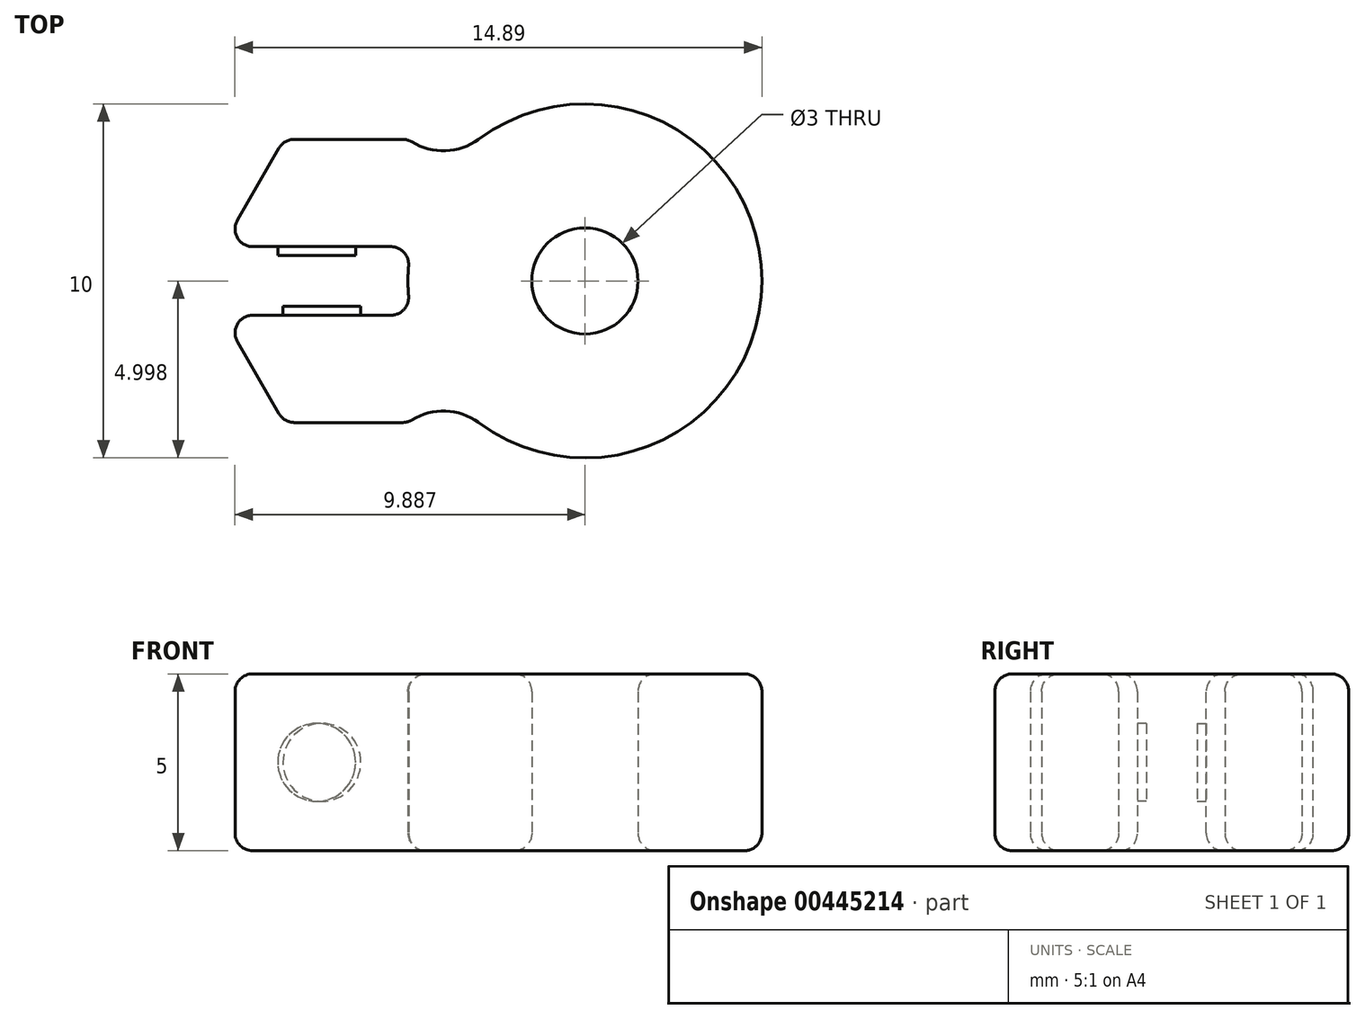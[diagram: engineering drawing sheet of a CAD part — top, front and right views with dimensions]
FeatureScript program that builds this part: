
annotation { "Feature Type Name" : "Feature", "Feature Type Description" : "" }
export const myFeature = defineFeature(function(context is Context, id is Id, definition is map)
    precondition{}
    {
        {
            var Q0;
            Q0=qCreatedBy(makeId("Top.planeOp"),FACE);
            var sketch = newSketch(context, id + "F0", { "sketchPlane" : qUnion([Q0])});
            skArc(sketch, "E0", {"start": v(-14.13, 11.46) * mm, "mid": v(-14.22, 10.49) * mm, "end": v(-14.13, 9.52) * mm});
            skCircle(sketch, "E1", {"center": v(-9.22, 10.49) * mm, "radius": 1.5 * mm});
            skArc(sketch, "E2", {"start": v(-14.22, 14.49) * mm, "mid": v(-13.22, 14.16) * mm, "end": v(-12.22, 14.49) * mm});
            skArc(sketch, "E3.MirrorCS", {"start": v(-14.22, 6.49) * mm, "mid": v(-13.22, 6.81) * mm, "end": v(-12.22, 6.49) * mm});
            skLineSegment(sketch, "E4", {"start": v(-14.22, 6.49) * mm, "end": v(-17.72, 6.49) * mm});
            skLineSegment(sketch, "E5", {"start": v(-17.72, 6.49) * mm, "end": v(-19.47, 9.52) * mm});
            skLineSegment(sketch, "E6.MirrorCS", {"start": v(-14.22, 14.49) * mm, "end": v(-17.72, 14.49) * mm});
            skLineSegment(sketch, "E7.MirrorCS", {"start": v(-17.72, 14.49) * mm, "end": v(-19.47, 11.46) * mm});
            skLineSegment(sketch, "E8", {"start": v(-19.47, 9.52) * mm, "end": v(-14.13, 9.52) * mm});
            skLineSegment(sketch, "E9", {"start": v(-19.47, 11.46) * mm, "end": v(-14.13, 11.46) * mm});
            skArc(sketch, "E10.trimOffspring", {"start": v(-12.22, 6.49) * mm, "mid": v(-4.22, 10.49) * mm, "end": v(-12.22, 14.49) * mm});
            skPoint(sketch, "E11.center.orphan", {"position": v(-16.8, 11.46) * mm});
            skLineSegment(sketch, "E12", {"start": v(-16.8, 11.46) * mm, "end": v(-19.47, 11.46) * mm});
            skPoint(sketch, "E13.center.orphan", {"position": v(-18.14, 11.46) * mm});
            skSolve(sketch);
        }
        {
            var Q0;
            Q0=makeQuery(id+"F0.imprint","IMPRINT",FACE,{"disambiguationData":[TD([[makeQuery(id+"F0.imprint","IMPRINT",EDGE,{"derivedFrom":sQuery(id+"F0.wireOp",EDGE,"E0")}),1.0]])]});
            extrude(context, id + "F1", {"entities" : qUnion([Q0]), "depth" : 5 * mm});
        }
        {
            var Q0;
            Q0=makeQuery(id+"F1.opExtrude","SWEPT_FACE",FACE,{"disambiguationData":[OSD([sQuery(id+"F0.wireOp",EDGE,"E9")])]});
            var sketch = newSketch(context, id + "F2", { "sketchPlane" : qUnion([Q0])});
            skCircle(sketch, "E14", {"center": v(-16.8, 2.5) * mm, "radius": 1.1 * mm});
            skSolve(sketch);
        }
        {
            var Q0;
            Q0=makeQuery(id+"F1.opExtrude","CAP_EDGE",EDGE,{"disambiguationData":[OSD([sQuery(id+"F0.wireOp",EDGE,"E0")])],"isStart":false});
            var Q1;
            Q1=makeQuery(id+"F1.opExtrude","CAP_EDGE",EDGE,{"disambiguationData":[OSD([sQuery(id+"F0.wireOp",EDGE,"E0")])],"isStart":true});
            var Q2;
            Q2=makeQuery(id+"F1.opExtrude","CAP_EDGE",EDGE,{"disambiguationData":[OSD([sQuery(id+"F0.wireOp",EDGE,"E2")])],"isStart":false});
            var Q3;
            Q3=makeQuery(id+"F1.opExtrude","SWEPT_EDGE",EDGE,{"disambiguationData":[OSD([sQuery(id+"F0.wireOp",EDGE,"E5"),sQuery(id+"F0.wireOp",EDGE,"E8")])]});
            var Q4;
            Q4=makeQuery(id+"F1.opExtrude","CAP_EDGE",EDGE,{"disambiguationData":[OSD([sQuery(id+"F0.wireOp",EDGE,"E5")])],"isStart":true});
            var Q5;
            Q5=makeQuery(id+"F1.opExtrude","SWEPT_EDGE",EDGE,{"disambiguationData":[OSD([sQuery(id+"F0.wireOp",EDGE,"E0"),sQuery(id+"F0.wireOp",EDGE,"E9")])]});
            var Q6;
            Q6=makeQuery(id+"F1.opExtrude","SWEPT_EDGE",EDGE,{"disambiguationData":[OSD([sQuery(id+"F0.wireOp",EDGE,"E6.MirrorCS"),sQuery(id+"F0.wireOp",EDGE,"E7.MirrorCS")])]});
            var Q7;
            Q7=makeQuery(id+"F1.opExtrude","CAP_EDGE",EDGE,{"disambiguationData":[OSD([sQuery(id+"F0.wireOp",EDGE,"E3.MirrorCS")])],"isStart":false});
            var Q8;
            Q8=makeQuery(id+"F1.opExtrude","CAP_EDGE",EDGE,{"disambiguationData":[OSD([sQuery(id+"F0.wireOp",EDGE,"E10.trimOffspring")])],"isStart":true});
            var Q9;
            Q9=makeQuery(id+"F1.opExtrude","SWEPT_EDGE",EDGE,{"disambiguationData":[OSD([sQuery(id+"F0.wireOp",EDGE,"E3.MirrorCS"),sQuery(id+"F0.wireOp",EDGE,"E4")])]});
            var Q10;
            Q10=makeQuery(id+"F1.opExtrude","CAP_EDGE",EDGE,{"disambiguationData":[OSD([sQuery(id+"F0.wireOp",EDGE,"E10.trimOffspring")])],"isStart":false});
            var Q11;
            Q11=makeQuery(id+"F1.opExtrude","CAP_EDGE",EDGE,{"disambiguationData":[OSD([sQuery(id+"F0.wireOp",EDGE,"E9"),sQuery(id+"F0.wireOp",EDGE,"E12")])],"isStart":true});
            var Q12;
            Q12=makeQuery(id+"F1.opExtrude","SWEPT_EDGE",EDGE,{"disambiguationData":[OSD([sQuery(id+"F0.wireOp",EDGE,"E4"),sQuery(id+"F0.wireOp",EDGE,"E5")])]});
            var Q13;
            Q13=makeQuery(id+"F1.opExtrude","CAP_EDGE",EDGE,{"disambiguationData":[OSD([sQuery(id+"F0.wireOp",EDGE,"E1")])],"isStart":false});
            var Q14;
            Q14=makeQuery(id+"F1.opExtrude","SWEPT_EDGE",EDGE,{"disambiguationData":[OSD([sQuery(id+"F0.wireOp",EDGE,"E2"),sQuery(id+"F0.wireOp",EDGE,"E10.trimOffspring")])]});
            var Q15;
            Q15=makeQuery(id+"F1.opExtrude","SWEPT_EDGE",EDGE,{"disambiguationData":[OSD([sQuery(id+"F0.wireOp",EDGE,"E7.MirrorCS"),sQuery(id+"F0.wireOp",EDGE,"E12")])]});
            var Q16;
            Q16=makeQuery(id+"F1.opExtrude","CAP_EDGE",EDGE,{"disambiguationData":[OSD([sQuery(id+"F0.wireOp",EDGE,"E5")])],"isStart":false});
            var Q17;
            Q17=makeQuery(id+"F1.opExtrude","CAP_EDGE",EDGE,{"disambiguationData":[OSD([sQuery(id+"F0.wireOp",EDGE,"E6.MirrorCS")])],"isStart":false});
            var Q18;
            Q18=makeQuery(id+"F1.opExtrude","CAP_EDGE",EDGE,{"disambiguationData":[OSD([sQuery(id+"F0.wireOp",EDGE,"E7.MirrorCS")])],"isStart":false});
            var Q19;
            Q19=makeQuery(id+"F1.opExtrude","CAP_EDGE",EDGE,{"disambiguationData":[OSD([sQuery(id+"F0.wireOp",EDGE,"E9"),sQuery(id+"F0.wireOp",EDGE,"E12")])],"isStart":false});
            var Q20;
            Q20=makeQuery(id+"F1.opExtrude","CAP_EDGE",EDGE,{"disambiguationData":[OSD([sQuery(id+"F0.wireOp",EDGE,"E2")])],"isStart":true});
            var Q21;
            Q21=makeQuery(id+"F1.opExtrude","SWEPT_EDGE",EDGE,{"disambiguationData":[OSD([sQuery(id+"F0.wireOp",EDGE,"E3.MirrorCS"),sQuery(id+"F0.wireOp",EDGE,"E10.trimOffspring")])]});
            var Q22;
            Q22=makeQuery(id+"F1.opExtrude","CAP_EDGE",EDGE,{"disambiguationData":[OSD([sQuery(id+"F0.wireOp",EDGE,"E8")])],"isStart":false});
            var Q23;
            Q23=makeQuery(id+"F1.opExtrude","CAP_EDGE",EDGE,{"disambiguationData":[OSD([sQuery(id+"F0.wireOp",EDGE,"E1")])],"isStart":true});
            var Q24;
            Q24=makeQuery(id+"F1.opExtrude","SWEPT_EDGE",EDGE,{"disambiguationData":[OSD([sQuery(id+"F0.wireOp",EDGE,"E2"),sQuery(id+"F0.wireOp",EDGE,"E6.MirrorCS")])]});
            var Q25;
            Q25=makeQuery(id+"F1.opExtrude","CAP_EDGE",EDGE,{"disambiguationData":[OSD([sQuery(id+"F0.wireOp",EDGE,"E3.MirrorCS")])],"isStart":true});
            var Q26;
            Q26=makeQuery(id+"F1.opExtrude","CAP_EDGE",EDGE,{"disambiguationData":[OSD([sQuery(id+"F0.wireOp",EDGE,"E6.MirrorCS")])],"isStart":true});
            var Q27;
            Q27=makeQuery(id+"F1.opExtrude","SWEPT_EDGE",EDGE,{"disambiguationData":[OSD([sQuery(id+"F0.wireOp",EDGE,"E0"),sQuery(id+"F0.wireOp",EDGE,"E8")])]});
            var Q28;
            Q28=makeQuery(id+"F1.opExtrude","CAP_EDGE",EDGE,{"disambiguationData":[OSD([sQuery(id+"F0.wireOp",EDGE,"E4")])],"isStart":true});
            var Q29;
            Q29=makeQuery(id+"F1.opExtrude","CAP_EDGE",EDGE,{"disambiguationData":[OSD([sQuery(id+"F0.wireOp",EDGE,"E4")])],"isStart":false});
            var Q30;
            Q30=makeQuery(id+"F1.opExtrude","CAP_EDGE",EDGE,{"disambiguationData":[OSD([sQuery(id+"F0.wireOp",EDGE,"E7.MirrorCS")])],"isStart":true});
            var Q31;
            Q31=makeQuery(id+"F1.opExtrude","CAP_EDGE",EDGE,{"disambiguationData":[OSD([sQuery(id+"F0.wireOp",EDGE,"E8")])],"isStart":true});
            fillet(context, id + "F3", {"entities" : qUnion([Q0, Q1, Q2, Q3, Q4, Q5, Q6, Q7, Q8, Q9, Q10, Q11, Q12, Q13, Q14, Q15, Q16, Q17, Q18, Q19, Q20, Q21, Q22, Q23, Q24, Q25, Q26, Q27, Q28, Q29, Q30, Q31]), "radius" : 0.5 * mm, "tangentPropagation" : true, "allowEdgeOverflow" : false});
        }
        {
            var Q0;
            Q0=makeQuery(id+"F2.imprint","IMPRINT",FACE,{"disambiguationData":[TD([[makeQuery(id+"F2.imprint","IMPRINT",EDGE,{"derivedFrom":sQuery(id+"F2.wireOp",EDGE,"E14")}),1.0]])]});
            extrude(context, id + "F4", {"entities" : qUnion([Q0]), "operationType" : NewBodyOperationType.ADD, "depth" : 0.25 * mm});
        }
        {
            var Q0;
            Q0=makeQuery(id+"F1.opExtrude","SWEPT_FACE",FACE,{"disambiguationData":[OSD([sQuery(id+"F0.wireOp",EDGE,"E8")])]});
            var sketch = newSketch(context, id + "F5", { "sketchPlane" : qUnion([Q0])});
            skCircle(sketch, "E15", {"center": v(16.65, 2.5) * mm, "radius": 1.1 * mm});
            skSolve(sketch);
        }
        {
            var Q0;
            Q0=makeQuery(id+"F5.imprint","IMPRINT",FACE,{"disambiguationData":[TD([[makeQuery(id+"F5.imprint","IMPRINT",EDGE,{"derivedFrom":sQuery(id+"F5.wireOp",EDGE,"E15")}),1.0]])]});
            extrude(context, id + "F6", {"entities" : qUnion([Q0]), "operationType" : NewBodyOperationType.ADD, "depth" : 0.25 * mm});
        }
    });
